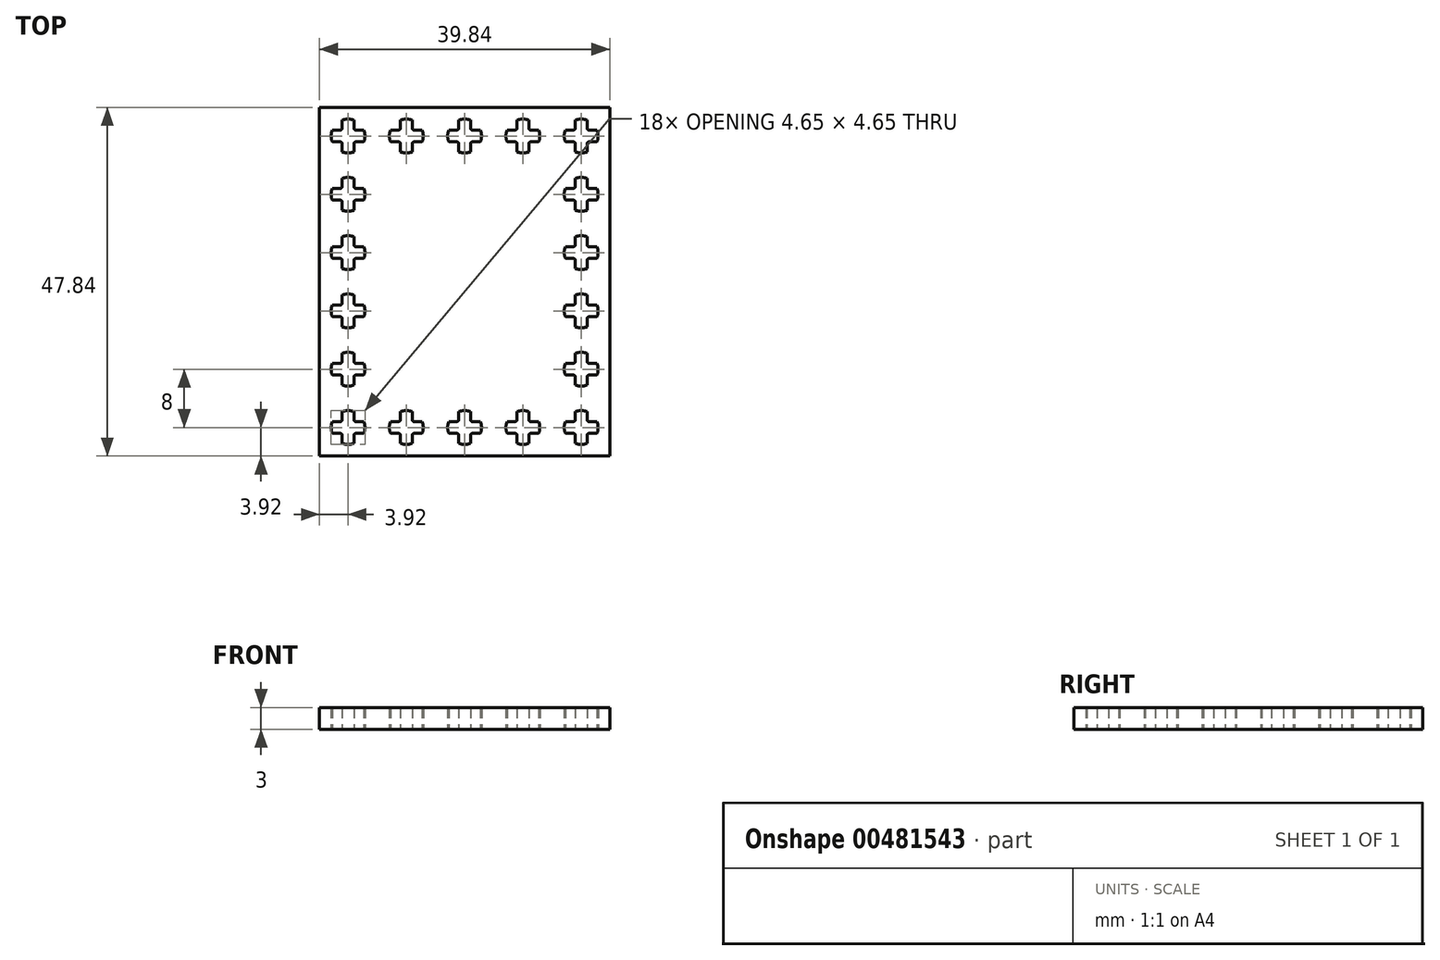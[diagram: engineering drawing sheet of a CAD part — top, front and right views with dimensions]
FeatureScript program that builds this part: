
annotation { "Feature Type Name" : "Feature", "Feature Type Description" : "" }
export const myFeature = defineFeature(function(context is Context, id is Id, definition is map)
    precondition{}
    {
        {
            var Q0;
            Q0=qCreatedBy(makeId("Top.planeOp"),FACE);
            var sketch = newSketch(context, id + "F0", { "sketchPlane" : qUnion([Q0])});
            skLineSegment(sketch, "E0.bottom", {"start": v(-20, 24) * mm, "end": v(20, 24) * mm, "construction": true});
            skLineSegment(sketch, "E0.top", {"start": v(-20, -24) * mm, "end": v(20, -24) * mm, "construction": true});
            skLineSegment(sketch, "E0.left", {"start": v(-20, 24) * mm, "end": v(-20, -24) * mm, "construction": true});
            skLineSegment(sketch, "E0.right", {"start": v(20, 24) * mm, "end": v(20, -24) * mm, "construction": true});
            skLineSegment(sketch, "E1", {"start": v(-16.8, 22.18) * mm, "end": v(-15.2, 22.18) * mm, "construction": true});
            skLineSegment(sketch, "E2", {"start": v(-15.2, 22.18) * mm, "end": v(-15.2, 21.1) * mm});
            skLineSegment(sketch, "E3", {"start": v(-14.9, 20.8) * mm, "end": v(-13.82, 20.8) * mm});
            skLineSegment(sketch, "E4", {"start": v(-13.82, 20.8) * mm, "end": v(-16, 20) * mm, "construction": true});
            skLineSegment(sketch, "E5", {"start": v(-16, 20) * mm, "end": v(-16.8, 22.18) * mm, "construction": true});
            skArc(sketch, "E6", {"start": v(-15.2, 22.18) * mm, "mid": v(-16, 22.33) * mm, "end": v(-16.8, 22.18) * mm});
            skArc(sketch, "E7", {"start": v(-15.2, 21.1) * mm, "mid": v(-15.11, 20.89) * mm, "end": v(-14.9, 20.8) * mm});
            skLineSegment(sketch, "E8", {"start": v(-15.2, 22.18) * mm, "end": v(-15.2, 20.8) * mm, "construction": true});
            skLineSegment(sketch, "E9", {"start": v(-15.2, 20.8) * mm, "end": v(-13.82, 20.8) * mm, "construction": true});
            skArc(sketch, "E10.1.0", {"start": v(-18.18, 20.8) * mm, "mid": v(-18.32, 20) * mm, "end": v(-18.18, 19.2) * mm});
            skArc(sketch, "E10.1.1", {"start": v(-17.1, 20.8) * mm, "mid": v(-16.89, 20.89) * mm, "end": v(-16.8, 21.1) * mm});
            skLineSegment(sketch, "E10.1.2", {"start": v(-18.18, 20.8) * mm, "end": v(-17.1, 20.8) * mm});
            skLineSegment(sketch, "E10.1.3", {"start": v(-16.8, 21.1) * mm, "end": v(-16.8, 22.18) * mm});
            skArc(sketch, "E10.2.0", {"start": v(-16.8, 17.82) * mm, "mid": v(-16, 17.68) * mm, "end": v(-15.2, 17.82) * mm});
            skArc(sketch, "E10.2.1", {"start": v(-16.8, 18.9) * mm, "mid": v(-16.89, 19.11) * mm, "end": v(-17.1, 19.2) * mm});
            skLineSegment(sketch, "E10.2.2", {"start": v(-16.8, 17.82) * mm, "end": v(-16.8, 18.9) * mm});
            skLineSegment(sketch, "E10.2.3", {"start": v(-17.1, 19.2) * mm, "end": v(-18.18, 19.2) * mm});
            skArc(sketch, "E10.3.0", {"start": v(-13.82, 19.2) * mm, "mid": v(-13.67, 20) * mm, "end": v(-13.82, 20.8) * mm});
            skArc(sketch, "E10.3.1", {"start": v(-14.9, 19.2) * mm, "mid": v(-15.11, 19.11) * mm, "end": v(-15.2, 18.9) * mm});
            skLineSegment(sketch, "E10.3.2", {"start": v(-13.82, 19.2) * mm, "end": v(-14.9, 19.2) * mm});
            skLineSegment(sketch, "E10.3.3", {"start": v(-15.2, 18.9) * mm, "end": v(-15.2, 17.82) * mm});
            skArc(sketch, "E11.0.1.0", {"start": v(-15.2, 14.18) * mm, "mid": v(-16, 14.32) * mm, "end": v(-16.8, 14.18) * mm});
            skArc(sketch, "E11.0.1.1", {"start": v(-14.9, 11.2) * mm, "mid": v(-15.11, 11.11) * mm, "end": v(-15.2, 10.9) * mm});
            skLineSegment(sketch, "E11.0.1.2", {"start": v(-13.82, 11.2) * mm, "end": v(-14.9, 11.2) * mm});
            skLineSegment(sketch, "E11.0.1.3", {"start": v(-17.1, 11.2) * mm, "end": v(-18.18, 11.2) * mm});
            skArc(sketch, "E11.0.1.4", {"start": v(-16.8, 10.9) * mm, "mid": v(-16.89, 11.11) * mm, "end": v(-17.1, 11.2) * mm});
            skLineSegment(sketch, "E11.0.1.5", {"start": v(-16.8, 13.1) * mm, "end": v(-16.8, 14.18) * mm});
            skLineSegment(sketch, "E11.0.1.6", {"start": v(-18.18, 12.8) * mm, "end": v(-17.1, 12.8) * mm});
            skArc(sketch, "E11.0.1.7", {"start": v(-17.1, 12.8) * mm, "mid": v(-16.89, 12.89) * mm, "end": v(-16.8, 13.1) * mm});
            skArc(sketch, "E11.0.1.8", {"start": v(-16.8, 9.82) * mm, "mid": v(-16, 9.67) * mm, "end": v(-15.2, 9.82) * mm});
            skArc(sketch, "E11.0.1.9", {"start": v(-18.18, 12.8) * mm, "mid": v(-18.32, 12) * mm, "end": v(-18.18, 11.2) * mm});
            skPoint(sketch, "E11.0.1.10", {"position": v(-16, 12) * mm});
            skLineSegment(sketch, "E11.0.1.11", {"start": v(-16.8, 9.82) * mm, "end": v(-16.8, 10.9) * mm});
            skArc(sketch, "E11.0.1.12", {"start": v(-13.82, 11.2) * mm, "mid": v(-13.67, 12) * mm, "end": v(-13.82, 12.8) * mm});
            skLineSegment(sketch, "E11.0.1.13", {"start": v(-15.2, 10.9) * mm, "end": v(-15.2, 9.82) * mm});
            skLineSegment(sketch, "E11.0.1.14", {"start": v(-15.2, 14.18) * mm, "end": v(-15.2, 13.1) * mm});
            skLineSegment(sketch, "E11.0.1.15", {"start": v(-14.9, 12.8) * mm, "end": v(-13.82, 12.8) * mm});
            skArc(sketch, "E11.0.1.16", {"start": v(-15.2, 13.1) * mm, "mid": v(-15.11, 12.89) * mm, "end": v(-14.9, 12.8) * mm});
            skArc(sketch, "E11.0.2.0", {"start": v(-15.2, 6.18) * mm, "mid": v(-16, 6.32) * mm, "end": v(-16.8, 6.18) * mm});
            skArc(sketch, "E11.0.2.1", {"start": v(-14.9, 3.2) * mm, "mid": v(-15.11, 3.11) * mm, "end": v(-15.2, 2.9) * mm});
            skLineSegment(sketch, "E11.0.2.2", {"start": v(-13.82, 3.2) * mm, "end": v(-14.9, 3.2) * mm});
            skLineSegment(sketch, "E11.0.2.3", {"start": v(-17.1, 3.2) * mm, "end": v(-18.18, 3.2) * mm});
            skArc(sketch, "E11.0.2.4", {"start": v(-16.8, 2.9) * mm, "mid": v(-16.89, 3.11) * mm, "end": v(-17.1, 3.2) * mm});
            skLineSegment(sketch, "E11.0.2.5", {"start": v(-16.8, 5.1) * mm, "end": v(-16.8, 6.18) * mm});
            skLineSegment(sketch, "E11.0.2.6", {"start": v(-18.18, 4.8) * mm, "end": v(-17.1, 4.8) * mm});
            skArc(sketch, "E11.0.2.7", {"start": v(-17.1, 4.8) * mm, "mid": v(-16.89, 4.89) * mm, "end": v(-16.8, 5.1) * mm});
            skArc(sketch, "E11.0.2.8", {"start": v(-16.8, 1.82) * mm, "mid": v(-16, 1.67) * mm, "end": v(-15.2, 1.82) * mm});
            skArc(sketch, "E11.0.2.9", {"start": v(-18.18, 4.8) * mm, "mid": v(-18.32, 4) * mm, "end": v(-18.18, 3.2) * mm});
            skPoint(sketch, "E11.0.2.10", {"position": v(-16, 4) * mm});
            skLineSegment(sketch, "E11.0.2.11", {"start": v(-16.8, 1.82) * mm, "end": v(-16.8, 2.9) * mm});
            skArc(sketch, "E11.0.2.12", {"start": v(-13.82, 3.2) * mm, "mid": v(-13.67, 4) * mm, "end": v(-13.82, 4.8) * mm});
            skLineSegment(sketch, "E11.0.2.13", {"start": v(-15.2, 2.9) * mm, "end": v(-15.2, 1.82) * mm});
            skLineSegment(sketch, "E11.0.2.14", {"start": v(-15.2, 6.18) * mm, "end": v(-15.2, 5.1) * mm});
            skLineSegment(sketch, "E11.0.2.15", {"start": v(-14.9, 4.8) * mm, "end": v(-13.82, 4.8) * mm});
            skArc(sketch, "E11.0.2.16", {"start": v(-15.2, 5.1) * mm, "mid": v(-15.11, 4.89) * mm, "end": v(-14.9, 4.8) * mm});
            skArc(sketch, "E11.0.3.0", {"start": v(-15.2, -1.82) * mm, "mid": v(-16, -1.68) * mm, "end": v(-16.8, -1.82) * mm});
            skArc(sketch, "E11.0.3.1", {"start": v(-14.9, -4.8) * mm, "mid": v(-15.11, -4.89) * mm, "end": v(-15.2, -5.1) * mm});
            skLineSegment(sketch, "E11.0.3.2", {"start": v(-13.82, -4.8) * mm, "end": v(-14.9, -4.8) * mm});
            skLineSegment(sketch, "E11.0.3.3", {"start": v(-17.1, -4.8) * mm, "end": v(-18.18, -4.8) * mm});
            skArc(sketch, "E11.0.3.4", {"start": v(-16.8, -5.1) * mm, "mid": v(-16.89, -4.89) * mm, "end": v(-17.1, -4.8) * mm});
            skLineSegment(sketch, "E11.0.3.5", {"start": v(-16.8, -2.9) * mm, "end": v(-16.8, -1.82) * mm});
            skLineSegment(sketch, "E11.0.3.6", {"start": v(-18.18, -3.2) * mm, "end": v(-17.1, -3.2) * mm});
            skArc(sketch, "E11.0.3.7", {"start": v(-17.1, -3.2) * mm, "mid": v(-16.89, -3.11) * mm, "end": v(-16.8, -2.9) * mm});
            skArc(sketch, "E11.0.3.8", {"start": v(-16.8, -6.18) * mm, "mid": v(-16, -6.33) * mm, "end": v(-15.2, -6.18) * mm});
            skArc(sketch, "E11.0.3.9", {"start": v(-18.18, -3.2) * mm, "mid": v(-18.32, -4) * mm, "end": v(-18.18, -4.8) * mm});
            skPoint(sketch, "E11.0.3.10", {"position": v(-16, -4) * mm});
            skLineSegment(sketch, "E11.0.3.11", {"start": v(-16.8, -6.18) * mm, "end": v(-16.8, -5.1) * mm});
            skArc(sketch, "E11.0.3.12", {"start": v(-13.82, -4.8) * mm, "mid": v(-13.67, -4) * mm, "end": v(-13.82, -3.2) * mm});
            skLineSegment(sketch, "E11.0.3.13", {"start": v(-15.2, -5.1) * mm, "end": v(-15.2, -6.18) * mm});
            skLineSegment(sketch, "E11.0.3.14", {"start": v(-15.2, -1.82) * mm, "end": v(-15.2, -2.9) * mm});
            skLineSegment(sketch, "E11.0.3.15", {"start": v(-14.9, -3.2) * mm, "end": v(-13.82, -3.2) * mm});
            skArc(sketch, "E11.0.3.16", {"start": v(-15.2, -2.9) * mm, "mid": v(-15.11, -3.11) * mm, "end": v(-14.9, -3.2) * mm});
            skArc(sketch, "E11.0.4.0", {"start": v(-15.2, -9.82) * mm, "mid": v(-16, -9.68) * mm, "end": v(-16.8, -9.82) * mm});
            skArc(sketch, "E11.0.4.1", {"start": v(-14.9, -12.8) * mm, "mid": v(-15.11, -12.89) * mm, "end": v(-15.2, -13.1) * mm});
            skLineSegment(sketch, "E11.0.4.2", {"start": v(-13.82, -12.8) * mm, "end": v(-14.9, -12.8) * mm});
            skLineSegment(sketch, "E11.0.4.3", {"start": v(-17.1, -12.8) * mm, "end": v(-18.18, -12.8) * mm});
            skArc(sketch, "E11.0.4.4", {"start": v(-16.8, -13.1) * mm, "mid": v(-16.89, -12.89) * mm, "end": v(-17.1, -12.8) * mm});
            skLineSegment(sketch, "E11.0.4.5", {"start": v(-16.8, -10.9) * mm, "end": v(-16.8, -9.82) * mm});
            skLineSegment(sketch, "E11.0.4.6", {"start": v(-18.18, -11.2) * mm, "end": v(-17.1, -11.2) * mm});
            skArc(sketch, "E11.0.4.7", {"start": v(-17.1, -11.2) * mm, "mid": v(-16.89, -11.11) * mm, "end": v(-16.8, -10.9) * mm});
            skArc(sketch, "E11.0.4.8", {"start": v(-16.8, -14.18) * mm, "mid": v(-16, -14.33) * mm, "end": v(-15.2, -14.18) * mm});
            skArc(sketch, "E11.0.4.9", {"start": v(-18.18, -11.2) * mm, "mid": v(-18.32, -12) * mm, "end": v(-18.18, -12.8) * mm});
            skPoint(sketch, "E11.0.4.10", {"position": v(-16, -12) * mm});
            skLineSegment(sketch, "E11.0.4.11", {"start": v(-16.8, -14.18) * mm, "end": v(-16.8, -13.1) * mm});
            skArc(sketch, "E11.0.4.12", {"start": v(-13.82, -12.8) * mm, "mid": v(-13.67, -12) * mm, "end": v(-13.82, -11.2) * mm});
            skLineSegment(sketch, "E11.0.4.13", {"start": v(-15.2, -13.1) * mm, "end": v(-15.2, -14.18) * mm});
            skLineSegment(sketch, "E11.0.4.14", {"start": v(-15.2, -9.82) * mm, "end": v(-15.2, -10.9) * mm});
            skLineSegment(sketch, "E11.0.4.15", {"start": v(-14.9, -11.2) * mm, "end": v(-13.82, -11.2) * mm});
            skArc(sketch, "E11.0.4.16", {"start": v(-15.2, -10.9) * mm, "mid": v(-15.11, -11.11) * mm, "end": v(-14.9, -11.2) * mm});
            skArc(sketch, "E11.1.0.0", {"start": v(-7.2, 22.18) * mm, "mid": v(-8, 22.33) * mm, "end": v(-8.8, 22.18) * mm});
            skArc(sketch, "E11.1.0.1", {"start": v(-6.9, 19.2) * mm, "mid": v(-7.11, 19.11) * mm, "end": v(-7.2, 18.9) * mm});
            skLineSegment(sketch, "E11.1.0.2", {"start": v(-5.82, 19.2) * mm, "end": v(-6.9, 19.2) * mm});
            skLineSegment(sketch, "E11.1.0.3", {"start": v(-9.1, 19.2) * mm, "end": v(-10.18, 19.2) * mm});
            skArc(sketch, "E11.1.0.4", {"start": v(-8.8, 18.9) * mm, "mid": v(-8.89, 19.11) * mm, "end": v(-9.1, 19.2) * mm});
            skLineSegment(sketch, "E11.1.0.5", {"start": v(-8.8, 21.1) * mm, "end": v(-8.8, 22.18) * mm});
            skLineSegment(sketch, "E11.1.0.6", {"start": v(-10.18, 20.8) * mm, "end": v(-9.1, 20.8) * mm});
            skArc(sketch, "E11.1.0.7", {"start": v(-9.1, 20.8) * mm, "mid": v(-8.89, 20.89) * mm, "end": v(-8.8, 21.1) * mm});
            skArc(sketch, "E11.1.0.8", {"start": v(-8.8, 17.82) * mm, "mid": v(-8, 17.68) * mm, "end": v(-7.2, 17.82) * mm});
            skArc(sketch, "E11.1.0.9", {"start": v(-10.18, 20.8) * mm, "mid": v(-10.33, 20) * mm, "end": v(-10.18, 19.2) * mm});
            skPoint(sketch, "E11.1.0.10", {"position": v(-8, 20) * mm});
            skLineSegment(sketch, "E11.1.0.11", {"start": v(-8.8, 17.82) * mm, "end": v(-8.8, 18.9) * mm});
            skArc(sketch, "E11.1.0.12", {"start": v(-5.82, 19.2) * mm, "mid": v(-5.68, 20) * mm, "end": v(-5.82, 20.8) * mm});
            skLineSegment(sketch, "E11.1.0.13", {"start": v(-7.2, 18.9) * mm, "end": v(-7.2, 17.82) * mm});
            skLineSegment(sketch, "E11.1.0.14", {"start": v(-7.2, 22.18) * mm, "end": v(-7.2, 21.1) * mm});
            skLineSegment(sketch, "E11.1.0.15", {"start": v(-6.9, 20.8) * mm, "end": v(-5.82, 20.8) * mm});
            skArc(sketch, "E11.1.0.16", {"start": v(-7.2, 21.1) * mm, "mid": v(-7.11, 20.89) * mm, "end": v(-6.9, 20.8) * mm});
            skArc(sketch, "E11.1.1.0", {"start": v(-7.2, 14.18) * mm, "mid": v(-8, 14.32) * mm, "end": v(-8.8, 14.18) * mm});
            skArc(sketch, "E11.1.1.1", {"start": v(-6.9, 11.2) * mm, "mid": v(-7.11, 11.11) * mm, "end": v(-7.2, 10.9) * mm});
            skLineSegment(sketch, "E11.1.1.2", {"start": v(-5.82, 11.2) * mm, "end": v(-6.9, 11.2) * mm});
            skLineSegment(sketch, "E11.1.1.3", {"start": v(-9.1, 11.2) * mm, "end": v(-10.18, 11.2) * mm});
            skArc(sketch, "E11.1.1.4", {"start": v(-8.8, 10.9) * mm, "mid": v(-8.89, 11.11) * mm, "end": v(-9.1, 11.2) * mm});
            skLineSegment(sketch, "E11.1.1.5", {"start": v(-8.8, 13.1) * mm, "end": v(-8.8, 14.18) * mm});
            skLineSegment(sketch, "E11.1.1.6", {"start": v(-10.18, 12.8) * mm, "end": v(-9.1, 12.8) * mm});
            skArc(sketch, "E11.1.1.7", {"start": v(-9.1, 12.8) * mm, "mid": v(-8.89, 12.89) * mm, "end": v(-8.8, 13.1) * mm});
            skArc(sketch, "E11.1.1.8", {"start": v(-8.8, 9.82) * mm, "mid": v(-8, 9.67) * mm, "end": v(-7.2, 9.82) * mm});
            skArc(sketch, "E11.1.1.9", {"start": v(-10.18, 12.8) * mm, "mid": v(-10.33, 12) * mm, "end": v(-10.18, 11.2) * mm});
            skPoint(sketch, "E11.1.1.10", {"position": v(-8, 12) * mm});
            skLineSegment(sketch, "E11.1.1.11", {"start": v(-8.8, 9.82) * mm, "end": v(-8.8, 10.9) * mm});
            skArc(sketch, "E11.1.1.12", {"start": v(-5.82, 11.2) * mm, "mid": v(-5.68, 12) * mm, "end": v(-5.82, 12.8) * mm});
            skLineSegment(sketch, "E11.1.1.13", {"start": v(-7.2, 10.9) * mm, "end": v(-7.2, 9.82) * mm});
            skLineSegment(sketch, "E11.1.1.14", {"start": v(-7.2, 14.18) * mm, "end": v(-7.2, 13.1) * mm});
            skLineSegment(sketch, "E11.1.1.15", {"start": v(-6.9, 12.8) * mm, "end": v(-5.82, 12.8) * mm});
            skArc(sketch, "E11.1.1.16", {"start": v(-7.2, 13.1) * mm, "mid": v(-7.11, 12.89) * mm, "end": v(-6.9, 12.8) * mm});
            skArc(sketch, "E11.1.2.0", {"start": v(-7.2, 6.18) * mm, "mid": v(-8, 6.32) * mm, "end": v(-8.8, 6.18) * mm});
            skArc(sketch, "E11.1.2.1", {"start": v(-6.9, 3.2) * mm, "mid": v(-7.11, 3.11) * mm, "end": v(-7.2, 2.9) * mm});
            skLineSegment(sketch, "E11.1.2.2", {"start": v(-5.82, 3.2) * mm, "end": v(-6.9, 3.2) * mm});
            skLineSegment(sketch, "E11.1.2.3", {"start": v(-9.1, 3.2) * mm, "end": v(-10.18, 3.2) * mm});
            skArc(sketch, "E11.1.2.4", {"start": v(-8.8, 2.9) * mm, "mid": v(-8.89, 3.11) * mm, "end": v(-9.1, 3.2) * mm});
            skLineSegment(sketch, "E11.1.2.5", {"start": v(-8.8, 5.1) * mm, "end": v(-8.8, 6.18) * mm});
            skLineSegment(sketch, "E11.1.2.6", {"start": v(-10.18, 4.8) * mm, "end": v(-9.1, 4.8) * mm});
            skArc(sketch, "E11.1.2.7", {"start": v(-9.1, 4.8) * mm, "mid": v(-8.89, 4.89) * mm, "end": v(-8.8, 5.1) * mm});
            skArc(sketch, "E11.1.2.8", {"start": v(-8.8, 1.82) * mm, "mid": v(-8, 1.67) * mm, "end": v(-7.2, 1.82) * mm});
            skArc(sketch, "E11.1.2.9", {"start": v(-10.18, 4.8) * mm, "mid": v(-10.33, 4) * mm, "end": v(-10.18, 3.2) * mm});
            skPoint(sketch, "E11.1.2.10", {"position": v(-8, 4) * mm});
            skLineSegment(sketch, "E11.1.2.11", {"start": v(-8.8, 1.82) * mm, "end": v(-8.8, 2.9) * mm});
            skArc(sketch, "E11.1.2.12", {"start": v(-5.82, 3.2) * mm, "mid": v(-5.68, 4) * mm, "end": v(-5.82, 4.8) * mm});
            skLineSegment(sketch, "E11.1.2.13", {"start": v(-7.2, 2.9) * mm, "end": v(-7.2, 1.82) * mm});
            skLineSegment(sketch, "E11.1.2.14", {"start": v(-7.2, 6.18) * mm, "end": v(-7.2, 5.1) * mm});
            skLineSegment(sketch, "E11.1.2.15", {"start": v(-6.9, 4.8) * mm, "end": v(-5.82, 4.8) * mm});
            skArc(sketch, "E11.1.2.16", {"start": v(-7.2, 5.1) * mm, "mid": v(-7.11, 4.89) * mm, "end": v(-6.9, 4.8) * mm});
            skArc(sketch, "E11.1.3.0", {"start": v(-7.2, -1.82) * mm, "mid": v(-8, -1.68) * mm, "end": v(-8.8, -1.82) * mm});
            skArc(sketch, "E11.1.3.1", {"start": v(-6.9, -4.8) * mm, "mid": v(-7.11, -4.89) * mm, "end": v(-7.2, -5.1) * mm});
            skLineSegment(sketch, "E11.1.3.2", {"start": v(-5.82, -4.8) * mm, "end": v(-6.9, -4.8) * mm});
            skLineSegment(sketch, "E11.1.3.3", {"start": v(-9.1, -4.8) * mm, "end": v(-10.18, -4.8) * mm});
            skArc(sketch, "E11.1.3.4", {"start": v(-8.8, -5.1) * mm, "mid": v(-8.89, -4.89) * mm, "end": v(-9.1, -4.8) * mm});
            skLineSegment(sketch, "E11.1.3.5", {"start": v(-8.8, -2.9) * mm, "end": v(-8.8, -1.82) * mm});
            skLineSegment(sketch, "E11.1.3.6", {"start": v(-10.18, -3.2) * mm, "end": v(-9.1, -3.2) * mm});
            skArc(sketch, "E11.1.3.7", {"start": v(-9.1, -3.2) * mm, "mid": v(-8.89, -3.11) * mm, "end": v(-8.8, -2.9) * mm});
            skArc(sketch, "E11.1.3.8", {"start": v(-8.8, -6.18) * mm, "mid": v(-8, -6.33) * mm, "end": v(-7.2, -6.18) * mm});
            skArc(sketch, "E11.1.3.9", {"start": v(-10.18, -3.2) * mm, "mid": v(-10.33, -4) * mm, "end": v(-10.18, -4.8) * mm});
            skPoint(sketch, "E11.1.3.10", {"position": v(-8, -4) * mm});
            skLineSegment(sketch, "E11.1.3.11", {"start": v(-8.8, -6.18) * mm, "end": v(-8.8, -5.1) * mm});
            skArc(sketch, "E11.1.3.12", {"start": v(-5.82, -4.8) * mm, "mid": v(-5.68, -4) * mm, "end": v(-5.82, -3.2) * mm});
            skLineSegment(sketch, "E11.1.3.13", {"start": v(-7.2, -5.1) * mm, "end": v(-7.2, -6.18) * mm});
            skLineSegment(sketch, "E11.1.3.14", {"start": v(-7.2, -1.82) * mm, "end": v(-7.2, -2.9) * mm});
            skLineSegment(sketch, "E11.1.3.15", {"start": v(-6.9, -3.2) * mm, "end": v(-5.82, -3.2) * mm});
            skArc(sketch, "E11.1.3.16", {"start": v(-7.2, -2.9) * mm, "mid": v(-7.11, -3.11) * mm, "end": v(-6.9, -3.2) * mm});
            skArc(sketch, "E11.1.4.0", {"start": v(-7.2, -9.82) * mm, "mid": v(-8, -9.68) * mm, "end": v(-8.8, -9.82) * mm});
            skArc(sketch, "E11.1.4.1", {"start": v(-6.9, -12.8) * mm, "mid": v(-7.11, -12.89) * mm, "end": v(-7.2, -13.1) * mm});
            skLineSegment(sketch, "E11.1.4.2", {"start": v(-5.82, -12.8) * mm, "end": v(-6.9, -12.8) * mm});
            skLineSegment(sketch, "E11.1.4.3", {"start": v(-9.1, -12.8) * mm, "end": v(-10.18, -12.8) * mm});
            skArc(sketch, "E11.1.4.4", {"start": v(-8.8, -13.1) * mm, "mid": v(-8.89, -12.89) * mm, "end": v(-9.1, -12.8) * mm});
            skLineSegment(sketch, "E11.1.4.5", {"start": v(-8.8, -10.9) * mm, "end": v(-8.8, -9.82) * mm});
            skLineSegment(sketch, "E11.1.4.6", {"start": v(-10.18, -11.2) * mm, "end": v(-9.1, -11.2) * mm});
            skArc(sketch, "E11.1.4.7", {"start": v(-9.1, -11.2) * mm, "mid": v(-8.89, -11.11) * mm, "end": v(-8.8, -10.9) * mm});
            skArc(sketch, "E11.1.4.8", {"start": v(-8.8, -14.18) * mm, "mid": v(-8, -14.33) * mm, "end": v(-7.2, -14.18) * mm});
            skArc(sketch, "E11.1.4.9", {"start": v(-10.18, -11.2) * mm, "mid": v(-10.33, -12) * mm, "end": v(-10.18, -12.8) * mm});
            skPoint(sketch, "E11.1.4.10", {"position": v(-8, -12) * mm});
            skLineSegment(sketch, "E11.1.4.11", {"start": v(-8.8, -14.18) * mm, "end": v(-8.8, -13.1) * mm});
            skArc(sketch, "E11.1.4.12", {"start": v(-5.82, -12.8) * mm, "mid": v(-5.68, -12) * mm, "end": v(-5.82, -11.2) * mm});
            skLineSegment(sketch, "E11.1.4.13", {"start": v(-7.2, -13.1) * mm, "end": v(-7.2, -14.18) * mm});
            skLineSegment(sketch, "E11.1.4.14", {"start": v(-7.2, -9.82) * mm, "end": v(-7.2, -10.9) * mm});
            skLineSegment(sketch, "E11.1.4.15", {"start": v(-6.9, -11.2) * mm, "end": v(-5.82, -11.2) * mm});
            skArc(sketch, "E11.1.4.16", {"start": v(-7.2, -10.9) * mm, "mid": v(-7.11, -11.11) * mm, "end": v(-6.9, -11.2) * mm});
            skArc(sketch, "E11.2.0.0", {"start": v(0.8, 22.18) * mm, "mid": v(0, 22.33) * mm, "end": v(-0.8, 22.18) * mm});
            skArc(sketch, "E11.2.0.1", {"start": v(1.1, 19.2) * mm, "mid": v(0.89, 19.11) * mm, "end": v(0.8, 18.9) * mm});
            skLineSegment(sketch, "E11.2.0.2", {"start": v(2.18, 19.2) * mm, "end": v(1.1, 19.2) * mm});
            skLineSegment(sketch, "E11.2.0.3", {"start": v(-1.1, 19.2) * mm, "end": v(-2.18, 19.2) * mm});
            skArc(sketch, "E11.2.0.4", {"start": v(-0.8, 18.9) * mm, "mid": v(-0.89, 19.11) * mm, "end": v(-1.1, 19.2) * mm});
            skLineSegment(sketch, "E11.2.0.5", {"start": v(-0.8, 21.1) * mm, "end": v(-0.8, 22.18) * mm});
            skLineSegment(sketch, "E11.2.0.6", {"start": v(-2.18, 20.8) * mm, "end": v(-1.1, 20.8) * mm});
            skArc(sketch, "E11.2.0.7", {"start": v(-1.1, 20.8) * mm, "mid": v(-0.89, 20.89) * mm, "end": v(-0.8, 21.1) * mm});
            skArc(sketch, "E11.2.0.8", {"start": v(-0.8, 17.82) * mm, "mid": v(0, 17.68) * mm, "end": v(0.8, 17.82) * mm});
            skArc(sketch, "E11.2.0.9", {"start": v(-2.18, 20.8) * mm, "mid": v(-2.33, 20) * mm, "end": v(-2.18, 19.2) * mm});
            skPoint(sketch, "E11.2.0.10", {"position": v(0, 20) * mm});
            skLineSegment(sketch, "E11.2.0.11", {"start": v(-0.8, 17.82) * mm, "end": v(-0.8, 18.9) * mm});
            skArc(sketch, "E11.2.0.12", {"start": v(2.18, 19.2) * mm, "mid": v(2.32, 20) * mm, "end": v(2.18, 20.8) * mm});
            skLineSegment(sketch, "E11.2.0.13", {"start": v(0.8, 18.9) * mm, "end": v(0.8, 17.82) * mm});
            skLineSegment(sketch, "E11.2.0.14", {"start": v(0.8, 22.18) * mm, "end": v(0.8, 21.1) * mm});
            skLineSegment(sketch, "E11.2.0.15", {"start": v(1.1, 20.8) * mm, "end": v(2.18, 20.8) * mm});
            skArc(sketch, "E11.2.0.16", {"start": v(0.8, 21.1) * mm, "mid": v(0.89, 20.89) * mm, "end": v(1.1, 20.8) * mm});
            skArc(sketch, "E11.2.1.0", {"start": v(0.8, 14.18) * mm, "mid": v(0, 14.32) * mm, "end": v(-0.8, 14.18) * mm});
            skArc(sketch, "E11.2.1.1", {"start": v(1.1, 11.2) * mm, "mid": v(0.89, 11.11) * mm, "end": v(0.8, 10.9) * mm});
            skLineSegment(sketch, "E11.2.1.2", {"start": v(2.18, 11.2) * mm, "end": v(1.1, 11.2) * mm});
            skLineSegment(sketch, "E11.2.1.3", {"start": v(-1.1, 11.2) * mm, "end": v(-2.18, 11.2) * mm});
            skArc(sketch, "E11.2.1.4", {"start": v(-0.8, 10.9) * mm, "mid": v(-0.89, 11.11) * mm, "end": v(-1.1, 11.2) * mm});
            skLineSegment(sketch, "E11.2.1.5", {"start": v(-0.8, 13.1) * mm, "end": v(-0.8, 14.18) * mm});
            skLineSegment(sketch, "E11.2.1.6", {"start": v(-2.18, 12.8) * mm, "end": v(-1.1, 12.8) * mm});
            skArc(sketch, "E11.2.1.7", {"start": v(-1.1, 12.8) * mm, "mid": v(-0.89, 12.89) * mm, "end": v(-0.8, 13.1) * mm});
            skArc(sketch, "E11.2.1.8", {"start": v(-0.8, 9.82) * mm, "mid": v(0, 9.67) * mm, "end": v(0.8, 9.82) * mm});
            skArc(sketch, "E11.2.1.9", {"start": v(-2.18, 12.8) * mm, "mid": v(-2.33, 12) * mm, "end": v(-2.18, 11.2) * mm});
            skPoint(sketch, "E11.2.1.10", {"position": v(0, 12) * mm});
            skLineSegment(sketch, "E11.2.1.11", {"start": v(-0.8, 9.82) * mm, "end": v(-0.8, 10.9) * mm});
            skArc(sketch, "E11.2.1.12", {"start": v(2.18, 11.2) * mm, "mid": v(2.32, 12) * mm, "end": v(2.18, 12.8) * mm});
            skLineSegment(sketch, "E11.2.1.13", {"start": v(0.8, 10.9) * mm, "end": v(0.8, 9.82) * mm});
            skLineSegment(sketch, "E11.2.1.14", {"start": v(0.8, 14.18) * mm, "end": v(0.8, 13.1) * mm});
            skLineSegment(sketch, "E11.2.1.15", {"start": v(1.1, 12.8) * mm, "end": v(2.18, 12.8) * mm});
            skArc(sketch, "E11.2.1.16", {"start": v(0.8, 13.1) * mm, "mid": v(0.89, 12.89) * mm, "end": v(1.1, 12.8) * mm});
            skArc(sketch, "E11.2.2.0", {"start": v(0.8, 6.18) * mm, "mid": v(0, 6.32) * mm, "end": v(-0.8, 6.18) * mm});
            skArc(sketch, "E11.2.2.1", {"start": v(1.1, 3.2) * mm, "mid": v(0.89, 3.11) * mm, "end": v(0.8, 2.9) * mm});
            skLineSegment(sketch, "E11.2.2.2", {"start": v(2.18, 3.2) * mm, "end": v(1.1, 3.2) * mm});
            skLineSegment(sketch, "E11.2.2.3", {"start": v(-1.1, 3.2) * mm, "end": v(-2.18, 3.2) * mm});
            skArc(sketch, "E11.2.2.4", {"start": v(-0.8, 2.9) * mm, "mid": v(-0.89, 3.11) * mm, "end": v(-1.1, 3.2) * mm});
            skLineSegment(sketch, "E11.2.2.5", {"start": v(-0.8, 5.1) * mm, "end": v(-0.8, 6.18) * mm});
            skLineSegment(sketch, "E11.2.2.6", {"start": v(-2.18, 4.8) * mm, "end": v(-1.1, 4.8) * mm});
            skArc(sketch, "E11.2.2.7", {"start": v(-1.1, 4.8) * mm, "mid": v(-0.89, 4.89) * mm, "end": v(-0.8, 5.1) * mm});
            skArc(sketch, "E11.2.2.8", {"start": v(-0.8, 1.82) * mm, "mid": v(0, 1.67) * mm, "end": v(0.8, 1.82) * mm});
            skArc(sketch, "E11.2.2.9", {"start": v(-2.18, 4.8) * mm, "mid": v(-2.33, 4) * mm, "end": v(-2.18, 3.2) * mm});
            skPoint(sketch, "E11.2.2.10", {"position": v(0, 4) * mm});
            skLineSegment(sketch, "E11.2.2.11", {"start": v(-0.8, 1.82) * mm, "end": v(-0.8, 2.9) * mm});
            skArc(sketch, "E11.2.2.12", {"start": v(2.18, 3.2) * mm, "mid": v(2.32, 4) * mm, "end": v(2.18, 4.8) * mm});
            skLineSegment(sketch, "E11.2.2.13", {"start": v(0.8, 2.9) * mm, "end": v(0.8, 1.82) * mm});
            skLineSegment(sketch, "E11.2.2.14", {"start": v(0.8, 6.18) * mm, "end": v(0.8, 5.1) * mm});
            skLineSegment(sketch, "E11.2.2.15", {"start": v(1.1, 4.8) * mm, "end": v(2.18, 4.8) * mm});
            skArc(sketch, "E11.2.2.16", {"start": v(0.8, 5.1) * mm, "mid": v(0.89, 4.89) * mm, "end": v(1.1, 4.8) * mm});
            skArc(sketch, "E11.2.3.0", {"start": v(0.8, -1.82) * mm, "mid": v(0, -1.68) * mm, "end": v(-0.8, -1.82) * mm});
            skArc(sketch, "E11.2.3.1", {"start": v(1.1, -4.8) * mm, "mid": v(0.89, -4.89) * mm, "end": v(0.8, -5.1) * mm});
            skLineSegment(sketch, "E11.2.3.2", {"start": v(2.18, -4.8) * mm, "end": v(1.1, -4.8) * mm});
            skLineSegment(sketch, "E11.2.3.3", {"start": v(-1.1, -4.8) * mm, "end": v(-2.18, -4.8) * mm});
            skArc(sketch, "E11.2.3.4", {"start": v(-0.8, -5.1) * mm, "mid": v(-0.89, -4.89) * mm, "end": v(-1.1, -4.8) * mm});
            skLineSegment(sketch, "E11.2.3.5", {"start": v(-0.8, -2.9) * mm, "end": v(-0.8, -1.82) * mm});
            skLineSegment(sketch, "E11.2.3.6", {"start": v(-2.18, -3.2) * mm, "end": v(-1.1, -3.2) * mm});
            skArc(sketch, "E11.2.3.7", {"start": v(-1.1, -3.2) * mm, "mid": v(-0.89, -3.11) * mm, "end": v(-0.8, -2.9) * mm});
            skArc(sketch, "E11.2.3.8", {"start": v(-0.8, -6.18) * mm, "mid": v(0, -6.33) * mm, "end": v(0.8, -6.18) * mm});
            skArc(sketch, "E11.2.3.9", {"start": v(-2.18, -3.2) * mm, "mid": v(-2.33, -4) * mm, "end": v(-2.18, -4.8) * mm});
            skPoint(sketch, "E11.2.3.10", {"position": v(0, -4) * mm});
            skLineSegment(sketch, "E11.2.3.11", {"start": v(-0.8, -6.18) * mm, "end": v(-0.8, -5.1) * mm});
            skArc(sketch, "E11.2.3.12", {"start": v(2.18, -4.8) * mm, "mid": v(2.32, -4) * mm, "end": v(2.18, -3.2) * mm});
            skLineSegment(sketch, "E11.2.3.13", {"start": v(0.8, -5.1) * mm, "end": v(0.8, -6.18) * mm});
            skLineSegment(sketch, "E11.2.3.14", {"start": v(0.8, -1.82) * mm, "end": v(0.8, -2.9) * mm});
            skLineSegment(sketch, "E11.2.3.15", {"start": v(1.1, -3.2) * mm, "end": v(2.18, -3.2) * mm});
            skArc(sketch, "E11.2.3.16", {"start": v(0.8, -2.9) * mm, "mid": v(0.89, -3.11) * mm, "end": v(1.1, -3.2) * mm});
            skArc(sketch, "E11.2.4.0", {"start": v(0.8, -9.82) * mm, "mid": v(0, -9.68) * mm, "end": v(-0.8, -9.82) * mm});
            skArc(sketch, "E11.2.4.1", {"start": v(1.1, -12.8) * mm, "mid": v(0.89, -12.89) * mm, "end": v(0.8, -13.1) * mm});
            skLineSegment(sketch, "E11.2.4.2", {"start": v(2.18, -12.8) * mm, "end": v(1.1, -12.8) * mm});
            skLineSegment(sketch, "E11.2.4.3", {"start": v(-1.1, -12.8) * mm, "end": v(-2.18, -12.8) * mm});
            skArc(sketch, "E11.2.4.4", {"start": v(-0.8, -13.1) * mm, "mid": v(-0.89, -12.89) * mm, "end": v(-1.1, -12.8) * mm});
            skLineSegment(sketch, "E11.2.4.5", {"start": v(-0.8, -10.9) * mm, "end": v(-0.8, -9.82) * mm});
            skLineSegment(sketch, "E11.2.4.6", {"start": v(-2.18, -11.2) * mm, "end": v(-1.1, -11.2) * mm});
            skArc(sketch, "E11.2.4.7", {"start": v(-1.1, -11.2) * mm, "mid": v(-0.89, -11.11) * mm, "end": v(-0.8, -10.9) * mm});
            skArc(sketch, "E11.2.4.8", {"start": v(-0.8, -14.18) * mm, "mid": v(0, -14.33) * mm, "end": v(0.8, -14.18) * mm});
            skArc(sketch, "E11.2.4.9", {"start": v(-2.18, -11.2) * mm, "mid": v(-2.33, -12) * mm, "end": v(-2.18, -12.8) * mm});
            skPoint(sketch, "E11.2.4.10", {"position": v(0, -12) * mm});
            skLineSegment(sketch, "E11.2.4.11", {"start": v(-0.8, -14.18) * mm, "end": v(-0.8, -13.1) * mm});
            skArc(sketch, "E11.2.4.12", {"start": v(2.18, -12.8) * mm, "mid": v(2.32, -12) * mm, "end": v(2.18, -11.2) * mm});
            skLineSegment(sketch, "E11.2.4.13", {"start": v(0.8, -13.1) * mm, "end": v(0.8, -14.18) * mm});
            skLineSegment(sketch, "E11.2.4.14", {"start": v(0.8, -9.82) * mm, "end": v(0.8, -10.9) * mm});
            skLineSegment(sketch, "E11.2.4.15", {"start": v(1.1, -11.2) * mm, "end": v(2.18, -11.2) * mm});
            skArc(sketch, "E11.2.4.16", {"start": v(0.8, -10.9) * mm, "mid": v(0.89, -11.11) * mm, "end": v(1.1, -11.2) * mm});
            skLineSegment(sketch, "E11.direction1", {"start": v(-16.8, 17.82) * mm, "end": v(-8.8, 17.82) * mm, "construction": true});
            skLineSegment(sketch, "E11.direction2", {"start": v(-16.8, 17.82) * mm, "end": v(-16.8, 9.82) * mm, "construction": true});
            skLineSegment(sketch, "E12.bottom", {"start": v(-19.93, 23.93) * mm, "end": v(19.93, 23.92) * mm});
            skLineSegment(sketch, "E12.top", {"start": v(-19.93, -23.92) * mm, "end": v(19.93, -23.93) * mm});
            skLineSegment(sketch, "E12.left", {"start": v(-19.93, 23.92) * mm, "end": v(-19.93, -23.93) * mm});
            skLineSegment(sketch, "E12.right", {"start": v(19.93, 23.92) * mm, "end": v(19.93, -23.93) * mm});
            skArc(sketch, "E13.0.0.5", {"start": v(-15.2, -17.82) * mm, "mid": v(-16, -17.68) * mm, "end": v(-16.8, -17.82) * mm});
            skArc(sketch, "E13.4.0.5", {"start": v(-14.9, -20.8) * mm, "mid": v(-15.11, -20.89) * mm, "end": v(-15.2, -21.1) * mm});
            skLineSegment(sketch, "E13.8.0.5", {"start": v(-13.82, -20.8) * mm, "end": v(-14.9, -20.8) * mm});
            skLineSegment(sketch, "E13.11.0.5", {"start": v(-17.1, -20.8) * mm, "end": v(-18.18, -20.8) * mm});
            skArc(sketch, "E13.14.0.5", {"start": v(-16.8, -21.1) * mm, "mid": v(-16.89, -20.89) * mm, "end": v(-17.1, -20.8) * mm});
            skLineSegment(sketch, "E13.18.0.5", {"start": v(-16.8, -18.9) * mm, "end": v(-16.8, -17.82) * mm});
            skLineSegment(sketch, "E13.21.0.5", {"start": v(-18.18, -19.2) * mm, "end": v(-17.1, -19.2) * mm});
            skArc(sketch, "E13.24.0.5", {"start": v(-17.1, -19.2) * mm, "mid": v(-16.89, -19.11) * mm, "end": v(-16.8, -18.9) * mm});
            skArc(sketch, "E13.28.0.5", {"start": v(-16.8, -22.18) * mm, "mid": v(-16, -22.33) * mm, "end": v(-15.2, -22.18) * mm});
            skArc(sketch, "E13.32.0.5", {"start": v(-18.18, -19.2) * mm, "mid": v(-18.32, -20) * mm, "end": v(-18.18, -20.8) * mm});
            skPoint(sketch, "E13.36.0.5", {"position": v(-16, -20) * mm});
            skLineSegment(sketch, "E13.37.0.5", {"start": v(-16.8, -22.18) * mm, "end": v(-16.8, -21.1) * mm});
            skArc(sketch, "E13.40.0.5", {"start": v(-13.82, -20.8) * mm, "mid": v(-13.67, -20) * mm, "end": v(-13.82, -19.2) * mm});
            skLineSegment(sketch, "E13.44.0.5", {"start": v(-15.2, -21.1) * mm, "end": v(-15.2, -22.18) * mm});
            skLineSegment(sketch, "E13.47.0.5", {"start": v(-15.2, -17.82) * mm, "end": v(-15.2, -18.9) * mm});
            skLineSegment(sketch, "E13.50.0.5", {"start": v(-14.9, -19.2) * mm, "end": v(-13.82, -19.2) * mm});
            skArc(sketch, "E13.53.0.5", {"start": v(-15.2, -18.9) * mm, "mid": v(-15.11, -19.11) * mm, "end": v(-14.9, -19.2) * mm});
            skArc(sketch, "E13.0.1.5", {"start": v(-7.2, -17.82) * mm, "mid": v(-8, -17.68) * mm, "end": v(-8.8, -17.82) * mm});
            skArc(sketch, "E13.4.1.5", {"start": v(-6.9, -20.8) * mm, "mid": v(-7.11, -20.89) * mm, "end": v(-7.2, -21.1) * mm});
            skLineSegment(sketch, "E13.8.1.5", {"start": v(-5.82, -20.8) * mm, "end": v(-6.9, -20.8) * mm});
            skLineSegment(sketch, "E13.11.1.5", {"start": v(-9.1, -20.8) * mm, "end": v(-10.18, -20.8) * mm});
            skArc(sketch, "E13.14.1.5", {"start": v(-8.8, -21.1) * mm, "mid": v(-8.89, -20.89) * mm, "end": v(-9.1, -20.8) * mm});
            skLineSegment(sketch, "E13.18.1.5", {"start": v(-8.8, -18.9) * mm, "end": v(-8.8, -17.82) * mm});
            skLineSegment(sketch, "E13.21.1.5", {"start": v(-10.18, -19.2) * mm, "end": v(-9.1, -19.2) * mm});
            skArc(sketch, "E13.24.1.5", {"start": v(-9.1, -19.2) * mm, "mid": v(-8.89, -19.11) * mm, "end": v(-8.8, -18.9) * mm});
            skArc(sketch, "E13.28.1.5", {"start": v(-8.8, -22.18) * mm, "mid": v(-8, -22.33) * mm, "end": v(-7.2, -22.18) * mm});
            skArc(sketch, "E13.32.1.5", {"start": v(-10.18, -19.2) * mm, "mid": v(-10.33, -20) * mm, "end": v(-10.18, -20.8) * mm});
            skPoint(sketch, "E13.36.1.5", {"position": v(-8, -20) * mm});
            skLineSegment(sketch, "E13.37.1.5", {"start": v(-8.8, -22.18) * mm, "end": v(-8.8, -21.1) * mm});
            skArc(sketch, "E13.40.1.5", {"start": v(-5.82, -20.8) * mm, "mid": v(-5.68, -20) * mm, "end": v(-5.82, -19.2) * mm});
            skLineSegment(sketch, "E13.44.1.5", {"start": v(-7.2, -21.1) * mm, "end": v(-7.2, -22.18) * mm});
            skLineSegment(sketch, "E13.47.1.5", {"start": v(-7.2, -17.82) * mm, "end": v(-7.2, -18.9) * mm});
            skLineSegment(sketch, "E13.50.1.5", {"start": v(-6.9, -19.2) * mm, "end": v(-5.82, -19.2) * mm});
            skArc(sketch, "E13.53.1.5", {"start": v(-7.2, -18.9) * mm, "mid": v(-7.11, -19.11) * mm, "end": v(-6.9, -19.2) * mm});
            skArc(sketch, "E13.0.2.5", {"start": v(0.8, -17.82) * mm, "mid": v(0, -17.68) * mm, "end": v(-0.8, -17.82) * mm});
            skArc(sketch, "E13.4.2.5", {"start": v(1.1, -20.8) * mm, "mid": v(0.89, -20.89) * mm, "end": v(0.8, -21.1) * mm});
            skLineSegment(sketch, "E13.8.2.5", {"start": v(2.18, -20.8) * mm, "end": v(1.1, -20.8) * mm});
            skLineSegment(sketch, "E13.11.2.5", {"start": v(-1.1, -20.8) * mm, "end": v(-2.18, -20.8) * mm});
            skArc(sketch, "E13.14.2.5", {"start": v(-0.8, -21.1) * mm, "mid": v(-0.89, -20.89) * mm, "end": v(-1.1, -20.8) * mm});
            skLineSegment(sketch, "E13.18.2.5", {"start": v(-0.8, -18.9) * mm, "end": v(-0.8, -17.82) * mm});
            skLineSegment(sketch, "E13.21.2.5", {"start": v(-2.18, -19.2) * mm, "end": v(-1.1, -19.2) * mm});
            skArc(sketch, "E13.24.2.5", {"start": v(-1.1, -19.2) * mm, "mid": v(-0.89, -19.11) * mm, "end": v(-0.8, -18.9) * mm});
            skArc(sketch, "E13.28.2.5", {"start": v(-0.8, -22.18) * mm, "mid": v(0, -22.33) * mm, "end": v(0.8, -22.18) * mm});
            skArc(sketch, "E13.32.2.5", {"start": v(-2.18, -19.2) * mm, "mid": v(-2.33, -20) * mm, "end": v(-2.18, -20.8) * mm});
            skPoint(sketch, "E13.36.2.5", {"position": v(0, -20) * mm});
            skLineSegment(sketch, "E13.37.2.5", {"start": v(-0.8, -22.18) * mm, "end": v(-0.8, -21.1) * mm});
            skArc(sketch, "E13.40.2.5", {"start": v(2.18, -20.8) * mm, "mid": v(2.32, -20) * mm, "end": v(2.18, -19.2) * mm});
            skLineSegment(sketch, "E13.44.2.5", {"start": v(0.8, -21.1) * mm, "end": v(0.8, -22.18) * mm});
            skLineSegment(sketch, "E13.47.2.5", {"start": v(0.8, -17.82) * mm, "end": v(0.8, -18.9) * mm});
            skLineSegment(sketch, "E13.50.2.5", {"start": v(1.1, -19.2) * mm, "end": v(2.18, -19.2) * mm});
            skArc(sketch, "E13.53.2.5", {"start": v(0.8, -18.9) * mm, "mid": v(0.89, -19.11) * mm, "end": v(1.1, -19.2) * mm});
            skArc(sketch, "E14.0.3.0", {"start": v(8.8, 22.18) * mm, "mid": v(8, 22.33) * mm, "end": v(7.2, 22.18) * mm});
            skArc(sketch, "E14.4.3.0", {"start": v(9.1, 19.2) * mm, "mid": v(8.89, 19.11) * mm, "end": v(8.8, 18.9) * mm});
            skLineSegment(sketch, "E14.8.3.0", {"start": v(10.18, 19.2) * mm, "end": v(9.1, 19.2) * mm});
            skLineSegment(sketch, "E14.11.3.0", {"start": v(6.9, 19.2) * mm, "end": v(5.82, 19.2) * mm});
            skArc(sketch, "E14.14.3.0", {"start": v(7.2, 18.9) * mm, "mid": v(7.11, 19.11) * mm, "end": v(6.9, 19.2) * mm});
            skLineSegment(sketch, "E14.18.3.0", {"start": v(7.2, 21.1) * mm, "end": v(7.2, 22.18) * mm});
            skLineSegment(sketch, "E14.21.3.0", {"start": v(5.82, 20.8) * mm, "end": v(6.9, 20.8) * mm});
            skArc(sketch, "E14.24.3.0", {"start": v(6.9, 20.8) * mm, "mid": v(7.11, 20.89) * mm, "end": v(7.2, 21.1) * mm});
            skArc(sketch, "E14.28.3.0", {"start": v(7.2, 17.82) * mm, "mid": v(8, 17.68) * mm, "end": v(8.8, 17.82) * mm});
            skArc(sketch, "E14.32.3.0", {"start": v(5.82, 20.8) * mm, "mid": v(5.67, 20) * mm, "end": v(5.82, 19.2) * mm});
            skPoint(sketch, "E14.36.3.0", {"position": v(8, 20) * mm});
            skLineSegment(sketch, "E14.37.3.0", {"start": v(7.2, 17.82) * mm, "end": v(7.2, 18.9) * mm});
            skArc(sketch, "E14.40.3.0", {"start": v(10.18, 19.2) * mm, "mid": v(10.32, 20) * mm, "end": v(10.18, 20.8) * mm});
            skLineSegment(sketch, "E14.44.3.0", {"start": v(8.8, 18.9) * mm, "end": v(8.8, 17.82) * mm});
            skLineSegment(sketch, "E14.47.3.0", {"start": v(8.8, 22.18) * mm, "end": v(8.8, 21.1) * mm});
            skLineSegment(sketch, "E14.50.3.0", {"start": v(9.1, 20.8) * mm, "end": v(10.18, 20.8) * mm});
            skArc(sketch, "E14.53.3.0", {"start": v(8.8, 21.1) * mm, "mid": v(8.89, 20.89) * mm, "end": v(9.1, 20.8) * mm});
            skArc(sketch, "E14.0.3.1", {"start": v(8.8, 14.18) * mm, "mid": v(8, 14.32) * mm, "end": v(7.2, 14.18) * mm});
            skArc(sketch, "E14.4.3.1", {"start": v(9.1, 11.2) * mm, "mid": v(8.89, 11.11) * mm, "end": v(8.8, 10.9) * mm});
            skLineSegment(sketch, "E14.8.3.1", {"start": v(10.18, 11.2) * mm, "end": v(9.1, 11.2) * mm});
            skLineSegment(sketch, "E14.11.3.1", {"start": v(6.9, 11.2) * mm, "end": v(5.82, 11.2) * mm});
            skArc(sketch, "E14.14.3.1", {"start": v(7.2, 10.9) * mm, "mid": v(7.11, 11.11) * mm, "end": v(6.9, 11.2) * mm});
            skLineSegment(sketch, "E14.18.3.1", {"start": v(7.2, 13.1) * mm, "end": v(7.2, 14.18) * mm});
            skLineSegment(sketch, "E14.21.3.1", {"start": v(5.82, 12.8) * mm, "end": v(6.9, 12.8) * mm});
            skArc(sketch, "E14.24.3.1", {"start": v(6.9, 12.8) * mm, "mid": v(7.11, 12.89) * mm, "end": v(7.2, 13.1) * mm});
            skArc(sketch, "E14.28.3.1", {"start": v(7.2, 9.82) * mm, "mid": v(8, 9.67) * mm, "end": v(8.8, 9.82) * mm});
            skArc(sketch, "E14.32.3.1", {"start": v(5.82, 12.8) * mm, "mid": v(5.67, 12) * mm, "end": v(5.82, 11.2) * mm});
            skPoint(sketch, "E14.36.3.1", {"position": v(8, 12) * mm});
            skLineSegment(sketch, "E14.37.3.1", {"start": v(7.2, 9.82) * mm, "end": v(7.2, 10.9) * mm});
            skArc(sketch, "E14.40.3.1", {"start": v(10.18, 11.2) * mm, "mid": v(10.32, 12) * mm, "end": v(10.18, 12.8) * mm});
            skLineSegment(sketch, "E14.44.3.1", {"start": v(8.8, 10.9) * mm, "end": v(8.8, 9.82) * mm});
            skLineSegment(sketch, "E14.47.3.1", {"start": v(8.8, 14.18) * mm, "end": v(8.8, 13.1) * mm});
            skLineSegment(sketch, "E14.50.3.1", {"start": v(9.1, 12.8) * mm, "end": v(10.18, 12.8) * mm});
            skArc(sketch, "E14.53.3.1", {"start": v(8.8, 13.1) * mm, "mid": v(8.89, 12.89) * mm, "end": v(9.1, 12.8) * mm});
            skArc(sketch, "E14.0.3.2", {"start": v(8.8, 6.18) * mm, "mid": v(8, 6.32) * mm, "end": v(7.2, 6.18) * mm});
            skArc(sketch, "E14.4.3.2", {"start": v(9.1, 3.2) * mm, "mid": v(8.89, 3.11) * mm, "end": v(8.8, 2.9) * mm});
            skLineSegment(sketch, "E14.8.3.2", {"start": v(10.18, 3.2) * mm, "end": v(9.1, 3.2) * mm});
            skLineSegment(sketch, "E14.11.3.2", {"start": v(6.9, 3.2) * mm, "end": v(5.82, 3.2) * mm});
            skArc(sketch, "E14.14.3.2", {"start": v(7.2, 2.9) * mm, "mid": v(7.11, 3.11) * mm, "end": v(6.9, 3.2) * mm});
            skLineSegment(sketch, "E14.18.3.2", {"start": v(7.2, 5.1) * mm, "end": v(7.2, 6.18) * mm});
            skLineSegment(sketch, "E14.21.3.2", {"start": v(5.82, 4.8) * mm, "end": v(6.9, 4.8) * mm});
            skArc(sketch, "E14.24.3.2", {"start": v(6.9, 4.8) * mm, "mid": v(7.11, 4.89) * mm, "end": v(7.2, 5.1) * mm});
            skArc(sketch, "E14.28.3.2", {"start": v(7.2, 1.82) * mm, "mid": v(8, 1.67) * mm, "end": v(8.8, 1.82) * mm});
            skArc(sketch, "E14.32.3.2", {"start": v(5.82, 4.8) * mm, "mid": v(5.67, 4) * mm, "end": v(5.82, 3.2) * mm});
            skPoint(sketch, "E14.36.3.2", {"position": v(8, 4) * mm});
            skLineSegment(sketch, "E14.37.3.2", {"start": v(7.2, 1.82) * mm, "end": v(7.2, 2.9) * mm});
            skArc(sketch, "E14.40.3.2", {"start": v(10.18, 3.2) * mm, "mid": v(10.32, 4) * mm, "end": v(10.18, 4.8) * mm});
            skLineSegment(sketch, "E14.44.3.2", {"start": v(8.8, 2.9) * mm, "end": v(8.8, 1.82) * mm});
            skLineSegment(sketch, "E14.47.3.2", {"start": v(8.8, 6.18) * mm, "end": v(8.8, 5.1) * mm});
            skLineSegment(sketch, "E14.50.3.2", {"start": v(9.1, 4.8) * mm, "end": v(10.18, 4.8) * mm});
            skArc(sketch, "E14.53.3.2", {"start": v(8.8, 5.1) * mm, "mid": v(8.89, 4.89) * mm, "end": v(9.1, 4.8) * mm});
            skArc(sketch, "E14.0.3.3", {"start": v(8.8, -1.82) * mm, "mid": v(8, -1.68) * mm, "end": v(7.2, -1.82) * mm});
            skArc(sketch, "E14.4.3.3", {"start": v(9.1, -4.8) * mm, "mid": v(8.89, -4.89) * mm, "end": v(8.8, -5.1) * mm});
            skLineSegment(sketch, "E14.8.3.3", {"start": v(10.18, -4.8) * mm, "end": v(9.1, -4.8) * mm});
            skLineSegment(sketch, "E14.11.3.3", {"start": v(6.9, -4.8) * mm, "end": v(5.82, -4.8) * mm});
            skArc(sketch, "E14.14.3.3", {"start": v(7.2, -5.1) * mm, "mid": v(7.11, -4.89) * mm, "end": v(6.9, -4.8) * mm});
            skLineSegment(sketch, "E14.18.3.3", {"start": v(7.2, -2.9) * mm, "end": v(7.2, -1.82) * mm});
            skLineSegment(sketch, "E14.21.3.3", {"start": v(5.82, -3.2) * mm, "end": v(6.9, -3.2) * mm});
            skArc(sketch, "E14.24.3.3", {"start": v(6.9, -3.2) * mm, "mid": v(7.11, -3.11) * mm, "end": v(7.2, -2.9) * mm});
            skArc(sketch, "E14.28.3.3", {"start": v(7.2, -6.18) * mm, "mid": v(8, -6.33) * mm, "end": v(8.8, -6.18) * mm});
            skArc(sketch, "E14.32.3.3", {"start": v(5.82, -3.2) * mm, "mid": v(5.67, -4) * mm, "end": v(5.82, -4.8) * mm});
            skPoint(sketch, "E14.36.3.3", {"position": v(8, -4) * mm});
            skLineSegment(sketch, "E14.37.3.3", {"start": v(7.2, -6.18) * mm, "end": v(7.2, -5.1) * mm});
            skArc(sketch, "E14.40.3.3", {"start": v(10.18, -4.8) * mm, "mid": v(10.32, -4) * mm, "end": v(10.18, -3.2) * mm});
            skLineSegment(sketch, "E14.44.3.3", {"start": v(8.8, -5.1) * mm, "end": v(8.8, -6.18) * mm});
            skLineSegment(sketch, "E14.47.3.3", {"start": v(8.8, -1.82) * mm, "end": v(8.8, -2.9) * mm});
            skLineSegment(sketch, "E14.50.3.3", {"start": v(9.1, -3.2) * mm, "end": v(10.18, -3.2) * mm});
            skArc(sketch, "E14.53.3.3", {"start": v(8.8, -2.9) * mm, "mid": v(8.89, -3.11) * mm, "end": v(9.1, -3.2) * mm});
            skArc(sketch, "E14.0.3.4", {"start": v(8.8, -9.82) * mm, "mid": v(8, -9.68) * mm, "end": v(7.2, -9.82) * mm});
            skArc(sketch, "E14.4.3.4", {"start": v(9.1, -12.8) * mm, "mid": v(8.89, -12.89) * mm, "end": v(8.8, -13.1) * mm});
            skLineSegment(sketch, "E14.8.3.4", {"start": v(10.18, -12.8) * mm, "end": v(9.1, -12.8) * mm});
            skLineSegment(sketch, "E14.11.3.4", {"start": v(6.9, -12.8) * mm, "end": v(5.82, -12.8) * mm});
            skArc(sketch, "E14.14.3.4", {"start": v(7.2, -13.1) * mm, "mid": v(7.11, -12.89) * mm, "end": v(6.9, -12.8) * mm});
            skLineSegment(sketch, "E14.18.3.4", {"start": v(7.2, -10.9) * mm, "end": v(7.2, -9.82) * mm});
            skLineSegment(sketch, "E14.21.3.4", {"start": v(5.82, -11.2) * mm, "end": v(6.9, -11.2) * mm});
            skArc(sketch, "E14.24.3.4", {"start": v(6.9, -11.2) * mm, "mid": v(7.11, -11.11) * mm, "end": v(7.2, -10.9) * mm});
            skArc(sketch, "E14.28.3.4", {"start": v(7.2, -14.18) * mm, "mid": v(8, -14.33) * mm, "end": v(8.8, -14.18) * mm});
            skArc(sketch, "E14.32.3.4", {"start": v(5.82, -11.2) * mm, "mid": v(5.67, -12) * mm, "end": v(5.82, -12.8) * mm});
            skPoint(sketch, "E14.36.3.4", {"position": v(8, -12) * mm});
            skLineSegment(sketch, "E14.37.3.4", {"start": v(7.2, -14.18) * mm, "end": v(7.2, -13.1) * mm});
            skArc(sketch, "E14.40.3.4", {"start": v(10.18, -12.8) * mm, "mid": v(10.32, -12) * mm, "end": v(10.18, -11.2) * mm});
            skLineSegment(sketch, "E14.44.3.4", {"start": v(8.8, -13.1) * mm, "end": v(8.8, -14.18) * mm});
            skLineSegment(sketch, "E14.47.3.4", {"start": v(8.8, -9.82) * mm, "end": v(8.8, -10.9) * mm});
            skLineSegment(sketch, "E14.50.3.4", {"start": v(9.1, -11.2) * mm, "end": v(10.18, -11.2) * mm});
            skArc(sketch, "E14.53.3.4", {"start": v(8.8, -10.9) * mm, "mid": v(8.89, -11.11) * mm, "end": v(9.1, -11.2) * mm});
            skArc(sketch, "E14.0.3.5", {"start": v(8.8, -17.82) * mm, "mid": v(8, -17.68) * mm, "end": v(7.2, -17.82) * mm});
            skArc(sketch, "E14.4.3.5", {"start": v(9.1, -20.8) * mm, "mid": v(8.89, -20.89) * mm, "end": v(8.8, -21.1) * mm});
            skLineSegment(sketch, "E14.8.3.5", {"start": v(10.18, -20.8) * mm, "end": v(9.1, -20.8) * mm});
            skLineSegment(sketch, "E14.11.3.5", {"start": v(6.9, -20.8) * mm, "end": v(5.82, -20.8) * mm});
            skArc(sketch, "E14.14.3.5", {"start": v(7.2, -21.1) * mm, "mid": v(7.11, -20.89) * mm, "end": v(6.9, -20.8) * mm});
            skLineSegment(sketch, "E14.18.3.5", {"start": v(7.2, -18.9) * mm, "end": v(7.2, -17.82) * mm});
            skLineSegment(sketch, "E14.21.3.5", {"start": v(5.82, -19.2) * mm, "end": v(6.9, -19.2) * mm});
            skArc(sketch, "E14.24.3.5", {"start": v(6.9, -19.2) * mm, "mid": v(7.11, -19.11) * mm, "end": v(7.2, -18.9) * mm});
            skArc(sketch, "E14.28.3.5", {"start": v(7.2, -22.18) * mm, "mid": v(8, -22.33) * mm, "end": v(8.8, -22.18) * mm});
            skArc(sketch, "E14.32.3.5", {"start": v(5.82, -19.2) * mm, "mid": v(5.67, -20) * mm, "end": v(5.82, -20.8) * mm});
            skPoint(sketch, "E14.36.3.5", {"position": v(8, -20) * mm});
            skLineSegment(sketch, "E14.37.3.5", {"start": v(7.2, -22.18) * mm, "end": v(7.2, -21.1) * mm});
            skArc(sketch, "E14.40.3.5", {"start": v(10.18, -20.8) * mm, "mid": v(10.32, -20) * mm, "end": v(10.18, -19.2) * mm});
            skLineSegment(sketch, "E14.44.3.5", {"start": v(8.8, -21.1) * mm, "end": v(8.8, -22.18) * mm});
            skLineSegment(sketch, "E14.47.3.5", {"start": v(8.8, -17.82) * mm, "end": v(8.8, -18.9) * mm});
            skLineSegment(sketch, "E14.50.3.5", {"start": v(9.1, -19.2) * mm, "end": v(10.18, -19.2) * mm});
            skArc(sketch, "E14.53.3.5", {"start": v(8.8, -18.9) * mm, "mid": v(8.89, -19.11) * mm, "end": v(9.1, -19.2) * mm});
            skArc(sketch, "E14.0.4.0", {"start": v(16.8, 22.18) * mm, "mid": v(16, 22.33) * mm, "end": v(15.2, 22.18) * mm});
            skArc(sketch, "E14.4.4.0", {"start": v(17.1, 19.2) * mm, "mid": v(16.89, 19.11) * mm, "end": v(16.8, 18.9) * mm});
            skLineSegment(sketch, "E14.8.4.0", {"start": v(18.18, 19.2) * mm, "end": v(17.1, 19.2) * mm});
            skLineSegment(sketch, "E14.11.4.0", {"start": v(14.9, 19.2) * mm, "end": v(13.82, 19.2) * mm});
            skArc(sketch, "E14.14.4.0", {"start": v(15.2, 18.9) * mm, "mid": v(15.11, 19.11) * mm, "end": v(14.9, 19.2) * mm});
            skLineSegment(sketch, "E14.18.4.0", {"start": v(15.2, 21.1) * mm, "end": v(15.2, 22.18) * mm});
            skLineSegment(sketch, "E14.21.4.0", {"start": v(13.82, 20.8) * mm, "end": v(14.9, 20.8) * mm});
            skArc(sketch, "E14.24.4.0", {"start": v(14.9, 20.8) * mm, "mid": v(15.11, 20.89) * mm, "end": v(15.2, 21.1) * mm});
            skArc(sketch, "E14.28.4.0", {"start": v(15.2, 17.82) * mm, "mid": v(16, 17.68) * mm, "end": v(16.8, 17.82) * mm});
            skArc(sketch, "E14.32.4.0", {"start": v(13.82, 20.8) * mm, "mid": v(13.67, 20) * mm, "end": v(13.82, 19.2) * mm});
            skPoint(sketch, "E14.36.4.0", {"position": v(16, 20) * mm});
            skLineSegment(sketch, "E14.37.4.0", {"start": v(15.2, 17.82) * mm, "end": v(15.2, 18.9) * mm});
            skArc(sketch, "E14.40.4.0", {"start": v(18.18, 19.2) * mm, "mid": v(18.32, 20) * mm, "end": v(18.18, 20.8) * mm});
            skLineSegment(sketch, "E14.44.4.0", {"start": v(16.8, 18.9) * mm, "end": v(16.8, 17.82) * mm});
            skLineSegment(sketch, "E14.47.4.0", {"start": v(16.8, 22.18) * mm, "end": v(16.8, 21.1) * mm});
            skLineSegment(sketch, "E14.50.4.0", {"start": v(17.1, 20.8) * mm, "end": v(18.18, 20.8) * mm});
            skArc(sketch, "E14.53.4.0", {"start": v(16.8, 21.1) * mm, "mid": v(16.89, 20.89) * mm, "end": v(17.1, 20.8) * mm});
            skArc(sketch, "E14.0.4.1", {"start": v(16.8, 14.18) * mm, "mid": v(16, 14.32) * mm, "end": v(15.2, 14.18) * mm});
            skArc(sketch, "E14.4.4.1", {"start": v(17.1, 11.2) * mm, "mid": v(16.89, 11.11) * mm, "end": v(16.8, 10.9) * mm});
            skLineSegment(sketch, "E14.8.4.1", {"start": v(18.18, 11.2) * mm, "end": v(17.1, 11.2) * mm});
            skLineSegment(sketch, "E14.11.4.1", {"start": v(14.9, 11.2) * mm, "end": v(13.82, 11.2) * mm});
            skArc(sketch, "E14.14.4.1", {"start": v(15.2, 10.9) * mm, "mid": v(15.11, 11.11) * mm, "end": v(14.9, 11.2) * mm});
            skLineSegment(sketch, "E14.18.4.1", {"start": v(15.2, 13.1) * mm, "end": v(15.2, 14.18) * mm});
            skLineSegment(sketch, "E14.21.4.1", {"start": v(13.82, 12.8) * mm, "end": v(14.9, 12.8) * mm});
            skArc(sketch, "E14.24.4.1", {"start": v(14.9, 12.8) * mm, "mid": v(15.11, 12.89) * mm, "end": v(15.2, 13.1) * mm});
            skArc(sketch, "E14.28.4.1", {"start": v(15.2, 9.82) * mm, "mid": v(16, 9.67) * mm, "end": v(16.8, 9.82) * mm});
            skArc(sketch, "E14.32.4.1", {"start": v(13.82, 12.8) * mm, "mid": v(13.67, 12) * mm, "end": v(13.82, 11.2) * mm});
            skPoint(sketch, "E14.36.4.1", {"position": v(16, 12) * mm});
            skLineSegment(sketch, "E14.37.4.1", {"start": v(15.2, 9.82) * mm, "end": v(15.2, 10.9) * mm});
            skArc(sketch, "E14.40.4.1", {"start": v(18.18, 11.2) * mm, "mid": v(18.32, 12) * mm, "end": v(18.18, 12.8) * mm});
            skLineSegment(sketch, "E14.44.4.1", {"start": v(16.8, 10.9) * mm, "end": v(16.8, 9.82) * mm});
            skLineSegment(sketch, "E14.47.4.1", {"start": v(16.8, 14.18) * mm, "end": v(16.8, 13.1) * mm});
            skLineSegment(sketch, "E14.50.4.1", {"start": v(17.1, 12.8) * mm, "end": v(18.18, 12.8) * mm});
            skArc(sketch, "E14.53.4.1", {"start": v(16.8, 13.1) * mm, "mid": v(16.89, 12.89) * mm, "end": v(17.1, 12.8) * mm});
            skArc(sketch, "E14.0.4.2", {"start": v(16.8, 6.18) * mm, "mid": v(16, 6.32) * mm, "end": v(15.2, 6.18) * mm});
            skArc(sketch, "E14.4.4.2", {"start": v(17.1, 3.2) * mm, "mid": v(16.89, 3.11) * mm, "end": v(16.8, 2.9) * mm});
            skLineSegment(sketch, "E14.8.4.2", {"start": v(18.18, 3.2) * mm, "end": v(17.1, 3.2) * mm});
            skLineSegment(sketch, "E14.11.4.2", {"start": v(14.9, 3.2) * mm, "end": v(13.82, 3.2) * mm});
            skArc(sketch, "E14.14.4.2", {"start": v(15.2, 2.9) * mm, "mid": v(15.11, 3.11) * mm, "end": v(14.9, 3.2) * mm});
            skLineSegment(sketch, "E14.18.4.2", {"start": v(15.2, 5.1) * mm, "end": v(15.2, 6.18) * mm});
            skLineSegment(sketch, "E14.21.4.2", {"start": v(13.82, 4.8) * mm, "end": v(14.9, 4.8) * mm});
            skArc(sketch, "E14.24.4.2", {"start": v(14.9, 4.8) * mm, "mid": v(15.11, 4.89) * mm, "end": v(15.2, 5.1) * mm});
            skArc(sketch, "E14.28.4.2", {"start": v(15.2, 1.82) * mm, "mid": v(16, 1.67) * mm, "end": v(16.8, 1.82) * mm});
            skArc(sketch, "E14.32.4.2", {"start": v(13.82, 4.8) * mm, "mid": v(13.67, 4) * mm, "end": v(13.82, 3.2) * mm});
            skPoint(sketch, "E14.36.4.2", {"position": v(16, 4) * mm});
            skLineSegment(sketch, "E14.37.4.2", {"start": v(15.2, 1.82) * mm, "end": v(15.2, 2.9) * mm});
            skArc(sketch, "E14.40.4.2", {"start": v(18.18, 3.2) * mm, "mid": v(18.32, 4) * mm, "end": v(18.18, 4.8) * mm});
            skLineSegment(sketch, "E14.44.4.2", {"start": v(16.8, 2.9) * mm, "end": v(16.8, 1.82) * mm});
            skLineSegment(sketch, "E14.47.4.2", {"start": v(16.8, 6.18) * mm, "end": v(16.8, 5.1) * mm});
            skLineSegment(sketch, "E14.50.4.2", {"start": v(17.1, 4.8) * mm, "end": v(18.18, 4.8) * mm});
            skArc(sketch, "E14.53.4.2", {"start": v(16.8, 5.1) * mm, "mid": v(16.89, 4.89) * mm, "end": v(17.1, 4.8) * mm});
            skArc(sketch, "E14.0.4.3", {"start": v(16.8, -1.82) * mm, "mid": v(16, -1.68) * mm, "end": v(15.2, -1.82) * mm});
            skArc(sketch, "E14.4.4.3", {"start": v(17.1, -4.8) * mm, "mid": v(16.89, -4.89) * mm, "end": v(16.8, -5.1) * mm});
            skLineSegment(sketch, "E14.8.4.3", {"start": v(18.18, -4.8) * mm, "end": v(17.1, -4.8) * mm});
            skLineSegment(sketch, "E14.11.4.3", {"start": v(14.9, -4.8) * mm, "end": v(13.82, -4.8) * mm});
            skArc(sketch, "E14.14.4.3", {"start": v(15.2, -5.1) * mm, "mid": v(15.11, -4.89) * mm, "end": v(14.9, -4.8) * mm});
            skLineSegment(sketch, "E14.18.4.3", {"start": v(15.2, -2.9) * mm, "end": v(15.2, -1.82) * mm});
            skLineSegment(sketch, "E14.21.4.3", {"start": v(13.82, -3.2) * mm, "end": v(14.9, -3.2) * mm});
            skArc(sketch, "E14.24.4.3", {"start": v(14.9, -3.2) * mm, "mid": v(15.11, -3.11) * mm, "end": v(15.2, -2.9) * mm});
            skArc(sketch, "E14.28.4.3", {"start": v(15.2, -6.18) * mm, "mid": v(16, -6.33) * mm, "end": v(16.8, -6.18) * mm});
            skArc(sketch, "E14.32.4.3", {"start": v(13.82, -3.2) * mm, "mid": v(13.67, -4) * mm, "end": v(13.82, -4.8) * mm});
            skPoint(sketch, "E14.36.4.3", {"position": v(16, -4) * mm});
            skLineSegment(sketch, "E14.37.4.3", {"start": v(15.2, -6.18) * mm, "end": v(15.2, -5.1) * mm});
            skArc(sketch, "E14.40.4.3", {"start": v(18.18, -4.8) * mm, "mid": v(18.32, -4) * mm, "end": v(18.18, -3.2) * mm});
            skLineSegment(sketch, "E14.44.4.3", {"start": v(16.8, -5.1) * mm, "end": v(16.8, -6.18) * mm});
            skLineSegment(sketch, "E14.47.4.3", {"start": v(16.8, -1.82) * mm, "end": v(16.8, -2.9) * mm});
            skLineSegment(sketch, "E14.50.4.3", {"start": v(17.1, -3.2) * mm, "end": v(18.18, -3.2) * mm});
            skArc(sketch, "E14.53.4.3", {"start": v(16.8, -2.9) * mm, "mid": v(16.89, -3.11) * mm, "end": v(17.1, -3.2) * mm});
            skArc(sketch, "E14.0.4.4", {"start": v(16.8, -9.82) * mm, "mid": v(16, -9.68) * mm, "end": v(15.2, -9.82) * mm});
            skArc(sketch, "E14.4.4.4", {"start": v(17.1, -12.8) * mm, "mid": v(16.89, -12.89) * mm, "end": v(16.8, -13.1) * mm});
            skLineSegment(sketch, "E14.8.4.4", {"start": v(18.18, -12.8) * mm, "end": v(17.1, -12.8) * mm});
            skLineSegment(sketch, "E14.11.4.4", {"start": v(14.9, -12.8) * mm, "end": v(13.82, -12.8) * mm});
            skArc(sketch, "E14.14.4.4", {"start": v(15.2, -13.1) * mm, "mid": v(15.11, -12.89) * mm, "end": v(14.9, -12.8) * mm});
            skLineSegment(sketch, "E14.18.4.4", {"start": v(15.2, -10.9) * mm, "end": v(15.2, -9.82) * mm});
            skLineSegment(sketch, "E14.21.4.4", {"start": v(13.82, -11.2) * mm, "end": v(14.9, -11.2) * mm});
            skArc(sketch, "E14.24.4.4", {"start": v(14.9, -11.2) * mm, "mid": v(15.11, -11.11) * mm, "end": v(15.2, -10.9) * mm});
            skArc(sketch, "E14.28.4.4", {"start": v(15.2, -14.18) * mm, "mid": v(16, -14.33) * mm, "end": v(16.8, -14.18) * mm});
            skArc(sketch, "E14.32.4.4", {"start": v(13.82, -11.2) * mm, "mid": v(13.67, -12) * mm, "end": v(13.82, -12.8) * mm});
            skPoint(sketch, "E14.36.4.4", {"position": v(16, -12) * mm});
            skLineSegment(sketch, "E14.37.4.4", {"start": v(15.2, -14.18) * mm, "end": v(15.2, -13.1) * mm});
            skArc(sketch, "E14.40.4.4", {"start": v(18.18, -12.8) * mm, "mid": v(18.32, -12) * mm, "end": v(18.18, -11.2) * mm});
            skLineSegment(sketch, "E14.44.4.4", {"start": v(16.8, -13.1) * mm, "end": v(16.8, -14.18) * mm});
            skLineSegment(sketch, "E14.47.4.4", {"start": v(16.8, -9.82) * mm, "end": v(16.8, -10.9) * mm});
            skLineSegment(sketch, "E14.50.4.4", {"start": v(17.1, -11.2) * mm, "end": v(18.18, -11.2) * mm});
            skArc(sketch, "E14.53.4.4", {"start": v(16.8, -10.9) * mm, "mid": v(16.89, -11.11) * mm, "end": v(17.1, -11.2) * mm});
            skArc(sketch, "E14.0.4.5", {"start": v(16.8, -17.82) * mm, "mid": v(16, -17.68) * mm, "end": v(15.2, -17.82) * mm});
            skArc(sketch, "E14.4.4.5", {"start": v(17.1, -20.8) * mm, "mid": v(16.89, -20.89) * mm, "end": v(16.8, -21.1) * mm});
            skLineSegment(sketch, "E14.8.4.5", {"start": v(18.18, -20.8) * mm, "end": v(17.1, -20.8) * mm});
            skLineSegment(sketch, "E14.11.4.5", {"start": v(14.9, -20.8) * mm, "end": v(13.82, -20.8) * mm});
            skArc(sketch, "E14.14.4.5", {"start": v(15.2, -21.1) * mm, "mid": v(15.11, -20.89) * mm, "end": v(14.9, -20.8) * mm});
            skLineSegment(sketch, "E14.18.4.5", {"start": v(15.2, -18.9) * mm, "end": v(15.2, -17.82) * mm});
            skLineSegment(sketch, "E14.21.4.5", {"start": v(13.82, -19.2) * mm, "end": v(14.9, -19.2) * mm});
            skArc(sketch, "E14.24.4.5", {"start": v(14.9, -19.2) * mm, "mid": v(15.11, -19.11) * mm, "end": v(15.2, -18.9) * mm});
            skArc(sketch, "E14.28.4.5", {"start": v(15.2, -22.18) * mm, "mid": v(16, -22.33) * mm, "end": v(16.8, -22.18) * mm});
            skArc(sketch, "E14.32.4.5", {"start": v(13.82, -19.2) * mm, "mid": v(13.67, -20) * mm, "end": v(13.82, -20.8) * mm});
            skPoint(sketch, "E14.36.4.5", {"position": v(16, -20) * mm});
            skLineSegment(sketch, "E14.37.4.5", {"start": v(15.2, -22.18) * mm, "end": v(15.2, -21.1) * mm});
            skArc(sketch, "E14.40.4.5", {"start": v(18.18, -20.8) * mm, "mid": v(18.32, -20) * mm, "end": v(18.18, -19.2) * mm});
            skLineSegment(sketch, "E14.44.4.5", {"start": v(16.8, -21.1) * mm, "end": v(16.8, -22.18) * mm});
            skLineSegment(sketch, "E14.47.4.5", {"start": v(16.8, -17.82) * mm, "end": v(16.8, -18.9) * mm});
            skLineSegment(sketch, "E14.50.4.5", {"start": v(17.1, -19.2) * mm, "end": v(18.18, -19.2) * mm});
            skArc(sketch, "E14.53.4.5", {"start": v(16.8, -18.9) * mm, "mid": v(16.89, -19.11) * mm, "end": v(17.1, -19.2) * mm});
            skSolve(sketch);
        }
        {
            var Q0;
            Q0=makeQuery(id+"F0.imprint","IMPRINT",FACE,{"disambiguationData":[TD([[makeQuery(id+"F0.imprint","IMPRINT",EDGE,{"derivedFrom":sQuery(id+"F0.wireOp",EDGE,"E2")}),1.0]])]});
            var Q1;
            Q1=makeQuery(id+"F0.imprint","IMPRINT",FACE,{"disambiguationData":[TD([[makeQuery(id+"F0.imprint","IMPRINT",EDGE,{"derivedFrom":sQuery(id+"F0.wireOp",EDGE,"E11.1.1.0")}),1.0]])]});
            var Q2;
            Q2=makeQuery(id+"F0.imprint","IMPRINT",FACE,{"disambiguationData":[TD([[makeQuery(id+"F0.imprint","IMPRINT",EDGE,{"derivedFrom":sQuery(id+"F0.wireOp",EDGE,"E11.1.2.0")}),1.0]])]});
            var Q3;
            Q3=makeQuery(id+"F0.imprint","IMPRINT",FACE,{"disambiguationData":[TD([[makeQuery(id+"F0.imprint","IMPRINT",EDGE,{"derivedFrom":sQuery(id+"F0.wireOp",EDGE,"E11.1.3.0")}),1.0]])]});
            var Q4;
            Q4=makeQuery(id+"F0.imprint","IMPRINT",FACE,{"disambiguationData":[TD([[makeQuery(id+"F0.imprint","IMPRINT",EDGE,{"derivedFrom":sQuery(id+"F0.wireOp",EDGE,"E11.1.4.0")}),1.0]])]});
            var Q5;
            Q5=makeQuery(id+"F0.imprint","IMPRINT",FACE,{"disambiguationData":[TD([[makeQuery(id+"F0.imprint","IMPRINT",EDGE,{"derivedFrom":sQuery(id+"F0.wireOp",EDGE,"E11.2.1.0")}),1.0]])]});
            var Q6;
            Q6=makeQuery(id+"F0.imprint","IMPRINT",FACE,{"disambiguationData":[TD([[makeQuery(id+"F0.imprint","IMPRINT",EDGE,{"derivedFrom":sQuery(id+"F0.wireOp",EDGE,"E11.2.2.0")}),1.0]])]});
            var Q7;
            Q7=makeQuery(id+"F0.imprint","IMPRINT",FACE,{"disambiguationData":[TD([[makeQuery(id+"F0.imprint","IMPRINT",EDGE,{"derivedFrom":sQuery(id+"F0.wireOp",EDGE,"E11.2.3.0")}),1.0]])]});
            var Q8;
            Q8=makeQuery(id+"F0.imprint","IMPRINT",FACE,{"disambiguationData":[TD([[makeQuery(id+"F0.imprint","IMPRINT",EDGE,{"derivedFrom":sQuery(id+"F0.wireOp",EDGE,"E11.2.4.0")}),1.0]])]});
            var Q9;
            Q9=makeQuery(id+"F0.imprint","IMPRINT",FACE,{"disambiguationData":[TD([[makeQuery(id+"F0.imprint","IMPRINT",EDGE,{"derivedFrom":sQuery(id+"F0.wireOp",EDGE,"E14.0.3.4")}),1.0]])]});
            var Q10;
            Q10=makeQuery(id+"F0.imprint","IMPRINT",FACE,{"disambiguationData":[TD([[makeQuery(id+"F0.imprint","IMPRINT",EDGE,{"derivedFrom":sQuery(id+"F0.wireOp",EDGE,"E14.0.3.3")}),1.0]])]});
            var Q11;
            Q11=makeQuery(id+"F0.imprint","IMPRINT",FACE,{"disambiguationData":[TD([[makeQuery(id+"F0.imprint","IMPRINT",EDGE,{"derivedFrom":sQuery(id+"F0.wireOp",EDGE,"E14.0.3.2")}),1.0]])]});
            var Q12;
            Q12=makeQuery(id+"F0.imprint","IMPRINT",FACE,{"disambiguationData":[TD([[makeQuery(id+"F0.imprint","IMPRINT",EDGE,{"derivedFrom":sQuery(id+"F0.wireOp",EDGE,"E14.0.3.1")}),1.0]])]});
            extrude(context, id + "F1", {"entities" : qUnion([Q0, Q1, Q2, Q3, Q4, Q5, Q6, Q7, Q8, Q9, Q10, Q11, Q12]), "depth" : 3 * mm, "offsetDistance" : 25 * mm});
        }
    });
